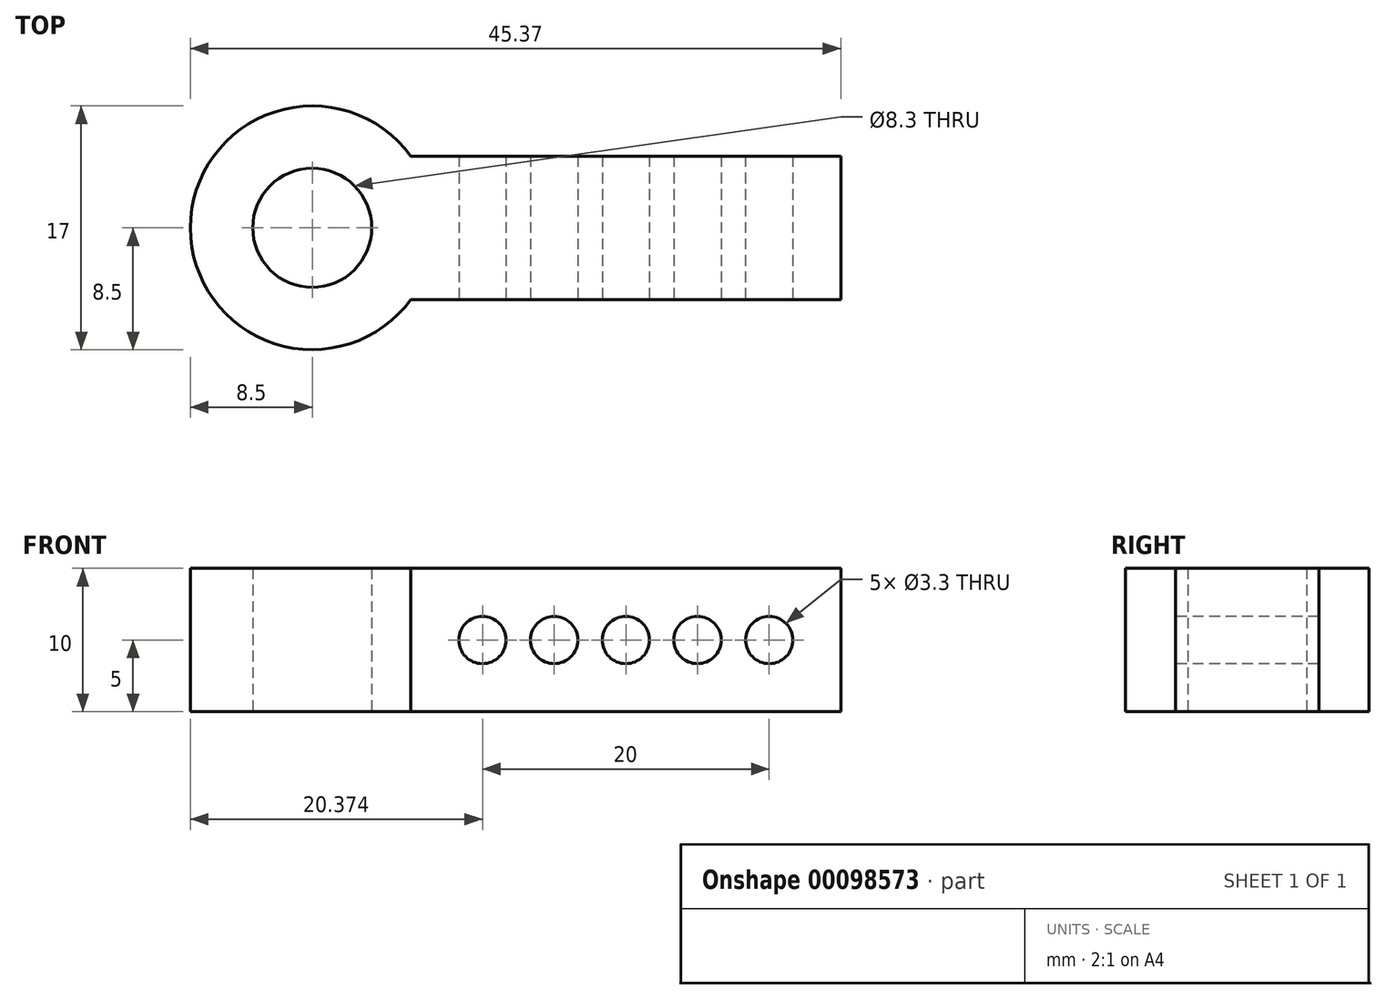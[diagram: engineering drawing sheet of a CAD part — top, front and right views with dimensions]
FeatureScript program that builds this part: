
annotation { "Feature Type Name" : "Feature", "Feature Type Description" : "" }
export const myFeature = defineFeature(function(context is Context, id is Id, definition is map)
    precondition{}
    {
        {
            var Q0;
            Q0=qCreatedBy(makeId("Top.planeOp"),FACE);
            var sketch = newSketch(context, id + "F0", { "sketchPlane" : qUnion([Q0])});
            skCircle(sketch, "E0", {"center": v(0, 0) * mm, "radius": 8.5 * mm});
            skCircle(sketch, "E1", {"center": v(0, 0) * mm, "radius": 4.15 * mm});
            skLineSegment(sketch, "E2.bottom", {"start": v(6.87, 5) * mm, "end": v(36.87, 5) * mm});
            skLineSegment(sketch, "E2.top", {"start": v(6.87, -5) * mm, "end": v(36.87, -5) * mm});
            skLineSegment(sketch, "E2.left", {"start": v(6.87, 5) * mm, "end": v(6.87, -5) * mm});
            skLineSegment(sketch, "E2.right", {"start": v(36.87, 5) * mm, "end": v(36.87, -5) * mm});
            skSolve(sketch);
        }
        {
            var Q0;
            Q0=makeQuery(id+"F0.imprint","IMPRINT",FACE,{"disambiguationData":[TD([[makeQuery(id+"F0.imprint","IMPRINT",EDGE,{"derivedFrom":sQuery(id+"F0.wireOp",EDGE,"E1")}),-1.0]])]});
            var Q1;
            {var subQ0=sQuery(id+"F0.wireOp",EDGE,"E2.left");Q1=makeQuery(id+"F0.imprint","IMPRINT",FACE,{"disambiguationData":[TD([[makeQuery(id+"F0.imprint","IMPRINT",EDGE,{"derivedFrom":subQ0}),1.0]])]});}
            var Q2;
            {var subQ1=sQuery(id+"F0.wireOp",EDGE,"E2.bottom");Q2=makeQuery(id+"F0.imprint","IMPRINT",FACE,{"disambiguationData":[TD([[makeQuery(id+"F0.imprint","IMPRINT",EDGE,{"derivedFrom":subQ1}),-1.0]])]});}
            extrude(context, id + "F1", {"entities" : qUnion([Q0, Q1, Q2]), "depth" : 10 * mm});
        }
        {
            var Q0;
            Q0=makeQuery(id+"F1.opExtrude","SWEPT_FACE",FACE,{"disambiguationData":[OSD([sQuery(id+"F0.wireOp",EDGE,"E2.top")])]});
            var sketch = newSketch(context, id + "F2", { "sketchPlane" : qUnion([Q0])});
            skCircle(sketch, "E3", {"center": v(31.87, 5) * mm, "radius": 1.65 * mm});
            skPoint(sketch, "E3.centerSnap0", {"position": v(36.87, 5) * mm});
            skCircle(sketch, "E4.1.0.0", {"center": v(26.87, 5) * mm, "radius": 1.65 * mm});
            skCircle(sketch, "E4.2.0.0", {"center": v(21.87, 5) * mm, "radius": 1.65 * mm});
            skCircle(sketch, "E4.3.0.0", {"center": v(16.87, 5) * mm, "radius": 1.65 * mm});
            skCircle(sketch, "E4.4.0.0", {"center": v(11.87, 5) * mm, "radius": 1.65 * mm});
            skLineSegment(sketch, "E4.direction1", {"start": v(31.87, 5) * mm, "end": v(26.87, 5) * mm, "construction": true});
            skSolve(sketch);
        }
        {
            var Q0;
            Q0=makeQuery(id+"F2.imprint","IMPRINT",FACE,{"disambiguationData":[TD([[makeQuery(id+"F2.imprint","IMPRINT",EDGE,{"derivedFrom":sQuery(id+"F2.wireOp",EDGE,"E4.4.0.0")}),1.0]])]});
            var Q1;
            Q1=makeQuery(id+"F2.imprint","IMPRINT",FACE,{"disambiguationData":[TD([[makeQuery(id+"F2.imprint","IMPRINT",EDGE,{"derivedFrom":sQuery(id+"F2.wireOp",EDGE,"E4.3.0.0")}),1.0]])]});
            var Q2;
            Q2=makeQuery(id+"F2.imprint","IMPRINT",FACE,{"disambiguationData":[TD([[makeQuery(id+"F2.imprint","IMPRINT",EDGE,{"derivedFrom":sQuery(id+"F2.wireOp",EDGE,"E4.2.0.0")}),1.0]])]});
            var Q3;
            Q3=makeQuery(id+"F2.imprint","IMPRINT",FACE,{"disambiguationData":[TD([[makeQuery(id+"F2.imprint","IMPRINT",EDGE,{"derivedFrom":sQuery(id+"F2.wireOp",EDGE,"E4.1.0.0")}),1.0]])]});
            var Q4;
            Q4=makeQuery(id+"F2.imprint","IMPRINT",FACE,{"disambiguationData":[TD([[makeQuery(id+"F2.imprint","IMPRINT",EDGE,{"derivedFrom":sQuery(id+"F2.wireOp",EDGE,"E3")}),1.0]])]});
            extrude(context, id + "F3", {"entities" : qUnion([Q0, Q1, Q2, Q3, Q4]), "operationType" : NewBodyOperationType.REMOVE, "oppositeDirection" : true, "depth" : 25 * mm});
        }
    });
